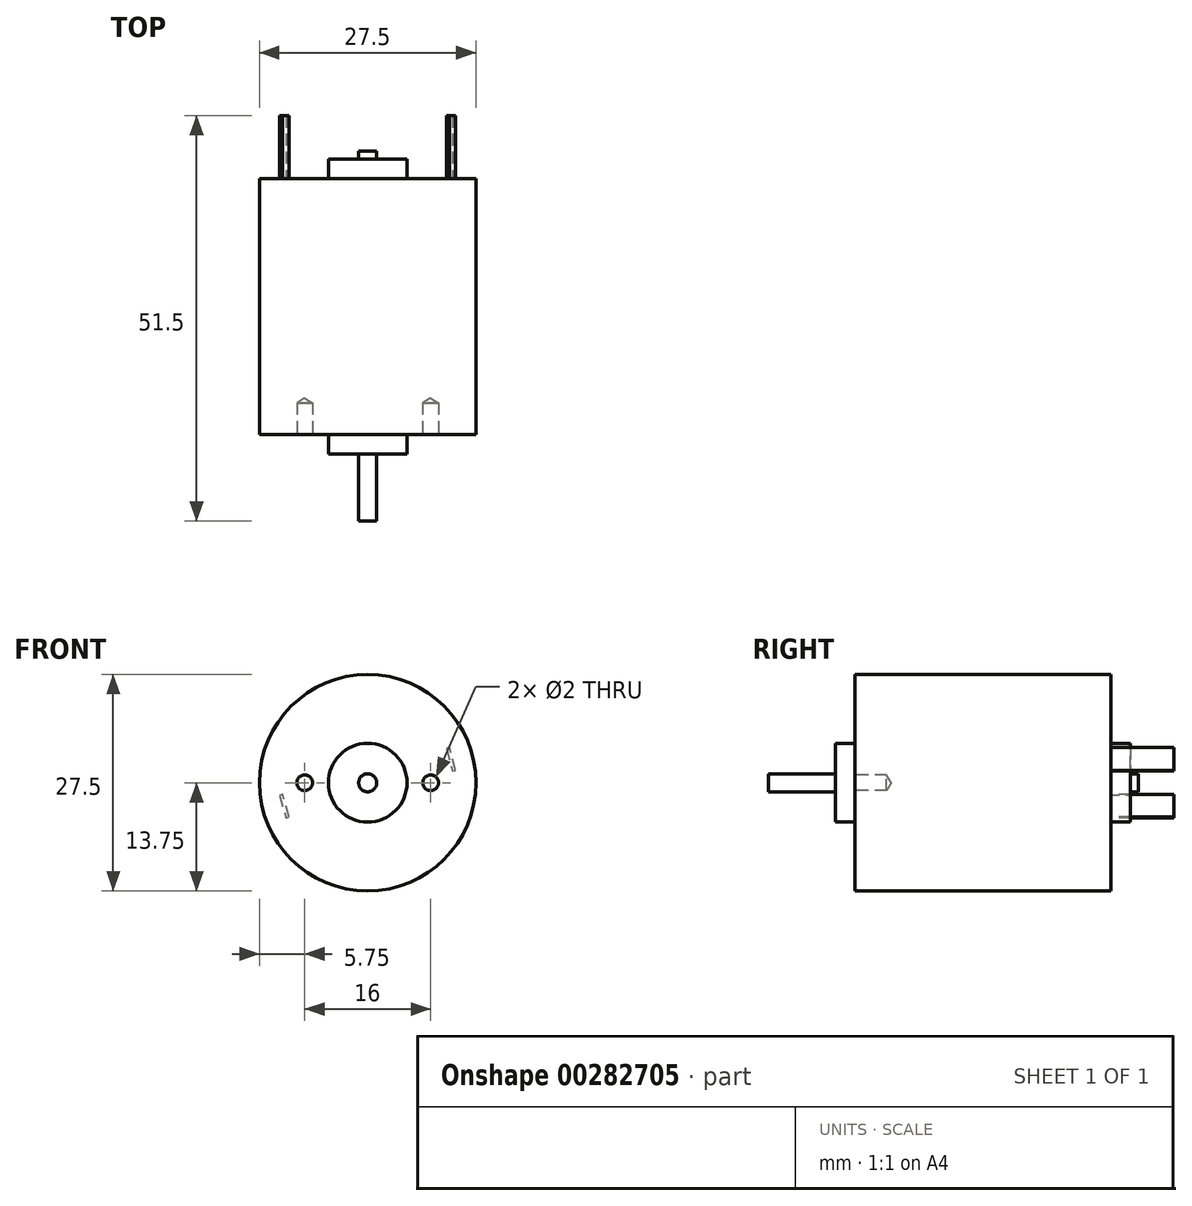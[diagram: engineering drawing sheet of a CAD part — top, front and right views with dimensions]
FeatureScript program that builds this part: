
annotation { "Feature Type Name" : "Feature", "Feature Type Description" : "" }
export const myFeature = defineFeature(function(context is Context, id is Id, definition is map)
    precondition{}
    {
        {
            var Q0;
            Q0=qCreatedBy(makeId("Front.planeOp"),FACE);
            var sketch = newSketch(context, id + "F0", { "sketchPlane" : qUnion([Q0])});
            skCircle(sketch, "E0", {"center": v(0, 0) * mm, "radius": 13.75 * mm});
            skSolve(sketch);
        }
        {
            var Q0;
            Q0=qSketchRegion(id+"F0",true);
            extrude(context, id + "F1", {"entities" : qUnion([Q0]), "oppositeDirection" : true, "depth" : 32.5 * mm});
        }
        {
            var Q0;
            Q0=makeQuery(id+"F1.opExtrude","CAP_FACE",FACE,{"disambiguationData":[OSD([sQuery(id+"F0.wireOp",EDGE,"E0")])],"isStart":true});
            var sketch = newSketch(context, id + "F2", { "sketchPlane" : qUnion([Q0])});
            skCircle(sketch, "E1", {"center": v(0, 0) * mm, "radius": 5 * mm});
            skSolve(sketch);
        }
        {
            var Q0;
            Q0=qSketchRegion(id+"F2",true);
            extrude(context, id + "F3", {"entities" : qUnion([Q0]), "operationType" : NewBodyOperationType.ADD, "depth" : 2.5 * mm});
        }
        {
            var Q0;
            Q0=makeQuery(id+"F1.opExtrude","CAP_FACE",FACE,{"disambiguationData":[OSD([sQuery(id+"F0.wireOp",EDGE,"E0")])],"isStart":false});
            var sketch = newSketch(context, id + "F4", { "sketchPlane" : qUnion([Q0])});
            skCircle(sketch, "E2", {"center": v(0, 0) * mm, "radius": 5 * mm});
            skSolve(sketch);
        }
        {
            var Q0;
            Q0=qSketchRegion(id+"F4",true);
            extrude(context, id + "F5", {"entities" : qUnion([Q0]), "operationType" : NewBodyOperationType.ADD, "depth" : 2.5 * mm});
        }
        {
            var Q0;
            Q0=makeQuery(id+"F1.opExtrude","CAP_FACE",FACE,{"disambiguationData":[OSD([sQuery(id+"F0.wireOp",EDGE,"E0")])],"isStart":true});
            var sketch = newSketch(context, id + "F6", { "sketchPlane" : qUnion([Q0])});
            skCircle(sketch, "E3", {"center": v(0, 0) * mm, "radius": 8 * mm, "construction": true});
            skCircle(sketch, "E4", {"center": v(8, 0) * mm, "radius": 1 * mm});
            skCircle(sketch, "E5.1.0", {"center": v(-8, 0) * mm, "radius": 1 * mm});
            skLineSegment(sketch, "E5.anchor1", {"start": v(0, 0) * mm, "end": v(8, 0) * mm, "construction": true});
            skLineSegment(sketch, "E5.anchor2", {"start": v(0, 0) * mm, "end": v(-8, 0) * mm, "construction": true});
            skSolve(sketch);
        }
        {
            var Q0;
            Q0=sQuery(id+"F6.wireOp",VERTEX,"E5.1.0.center");
            var Q1;
            Q1=sQuery(id+"F6.wireOp",VERTEX,"E4.center");
            var Q2;
            Q2=makeQuery(id+"F1.opExtrude","SWEPT_BODY",BODY,{"disambiguationData":[OSD([sQuery(id+"F0.wireOp",EDGE,"E0")])]});
            hole(context, id + "F7", {"style" : HoleStyle.SIMPLE, "endStyle" : HoleEndStyle.BLIND, "holeDiameter" : 2 * mm, "holeDepth" : 4 * mm, "locations" : qUnion([Q0, Q1]), "scope" : qUnion([Q2])});
        }
        {
            var Q0;
            Q0=makeQuery(id+"F1.opExtrude","CAP_FACE",FACE,{"disambiguationData":[OSD([sQuery(id+"F0.wireOp",EDGE,"E0")])],"isStart":false});
            var sketch = newSketch(context, id + "F8", { "sketchPlane" : qUnion([Q0])});
            skCircle(sketch, "E6", {"center": v(0, 0) * mm, "radius": 11 * mm, "construction": true});
            skCircle(sketch, "E7", {"center": v(11, 0) * mm, "radius": 3 * mm, "construction": true});
            skLineSegment(sketch, "E8", {"start": v(11, -1.53) * mm, "end": v(11.19, -1.58) * mm});
            skLineSegment(sketch, "E9", {"start": v(11.19, -1.58) * mm, "end": v(10.38, -4.47) * mm});
            skLineSegment(sketch, "E10", {"start": v(10.38, -4.47) * mm, "end": v(10, -4.36) * mm});
            skLineSegment(sketch, "E11", {"start": v(10, -4.36) * mm, "end": v(10.8, -1.47) * mm});
            skLineSegment(sketch, "E12", {"start": v(10.8, -1.47) * mm, "end": v(11.19, -1.58) * mm});
            skLineSegment(sketch, "E13.1.0", {"start": v(-10, 4.36) * mm, "end": v(-10.8, 1.47) * mm});
            skLineSegment(sketch, "E13.1.1", {"start": v(-11.19, 1.58) * mm, "end": v(-10.38, 4.47) * mm});
            skLineSegment(sketch, "E13.1.2", {"start": v(-10.38, 4.47) * mm, "end": v(-10, 4.36) * mm});
            skLineSegment(sketch, "E13.1.3", {"start": v(-10.8, 1.47) * mm, "end": v(-11.19, 1.58) * mm});
            skLineSegment(sketch, "E13.1.4", {"start": v(-11, 1.53) * mm, "end": v(-11.19, 1.58) * mm});
            skSolve(sketch);
        }
        {
            var Q0;
            Q0=qSketchRegion(id+"F8",true);
            extrude(context, id + "F9", {"entities" : qUnion([Q0]), "operationType" : NewBodyOperationType.ADD, "depth" : 8 * mm});
        }
        {
            var Q0;
            Q0=makeQuery(id+"F3.opExtrude","CAP_FACE",FACE,{"disambiguationData":[OSD([sQuery(id+"F2.wireOp",EDGE,"E1")])],"isStart":false});
            var sketch = newSketch(context, id + "F10", { "sketchPlane" : qUnion([Q0])});
            skCircle(sketch, "E14", {"center": v(0, 0) * mm, "radius": 1.15 * mm});
            skSolve(sketch);
        }
        {
            var Q0;
            Q0=qSketchRegion(id+"F10",true);
            extrude(context, id + "F11", {"entities" : qUnion([Q0]), "operationType" : NewBodyOperationType.REMOVE, "endBound" : BoundingType.THROUGH_ALL, "oppositeDirection" : true, "depth" : 25 * mm});
        }
        {
            var Q0;
            Q0=makeQuery(id+"F3.opExtrude","CAP_FACE",FACE,{"disambiguationData":[OSD([sQuery(id+"F2.wireOp",EDGE,"E1")])],"isStart":false});
            var sketch = newSketch(context, id + "F12", { "sketchPlane" : qUnion([Q0])});
            skCircle(sketch, "E15", {"center": v(0, 0) * mm, "radius": 1.15 * mm});
            skSolve(sketch);
        }
        {
            var Q0;
            Q0=qSketchRegion(id+"F12",true);
            extrude(context, id + "F13", {"entities" : qUnion([Q0]), "oppositeDirection" : true, "depth" : 38.5 * mm});
        }
        {
            var Q0;
            Q0=makeQuery(id+"F13.opExtrude","CAP_FACE",FACE,{"disambiguationData":[OSD([sQuery(id+"F12.wireOp",EDGE,"E15")])],"isStart":true});
            var sketch = newSketch(context, id + "F14", { "sketchPlane" : qUnion([Q0])});
            skCircle(sketch, "E16", {"center": v(0, 0) * mm, "radius": 1.15 * mm});
            skSolve(sketch);
        }
        {
            var Q0;
            Q0=qSketchRegion(id+"F14",true);
            extrude(context, id + "F15", {"entities" : qUnion([Q0]), "operationType" : NewBodyOperationType.ADD, "depth" : 8.5 * mm});
        }
    });
